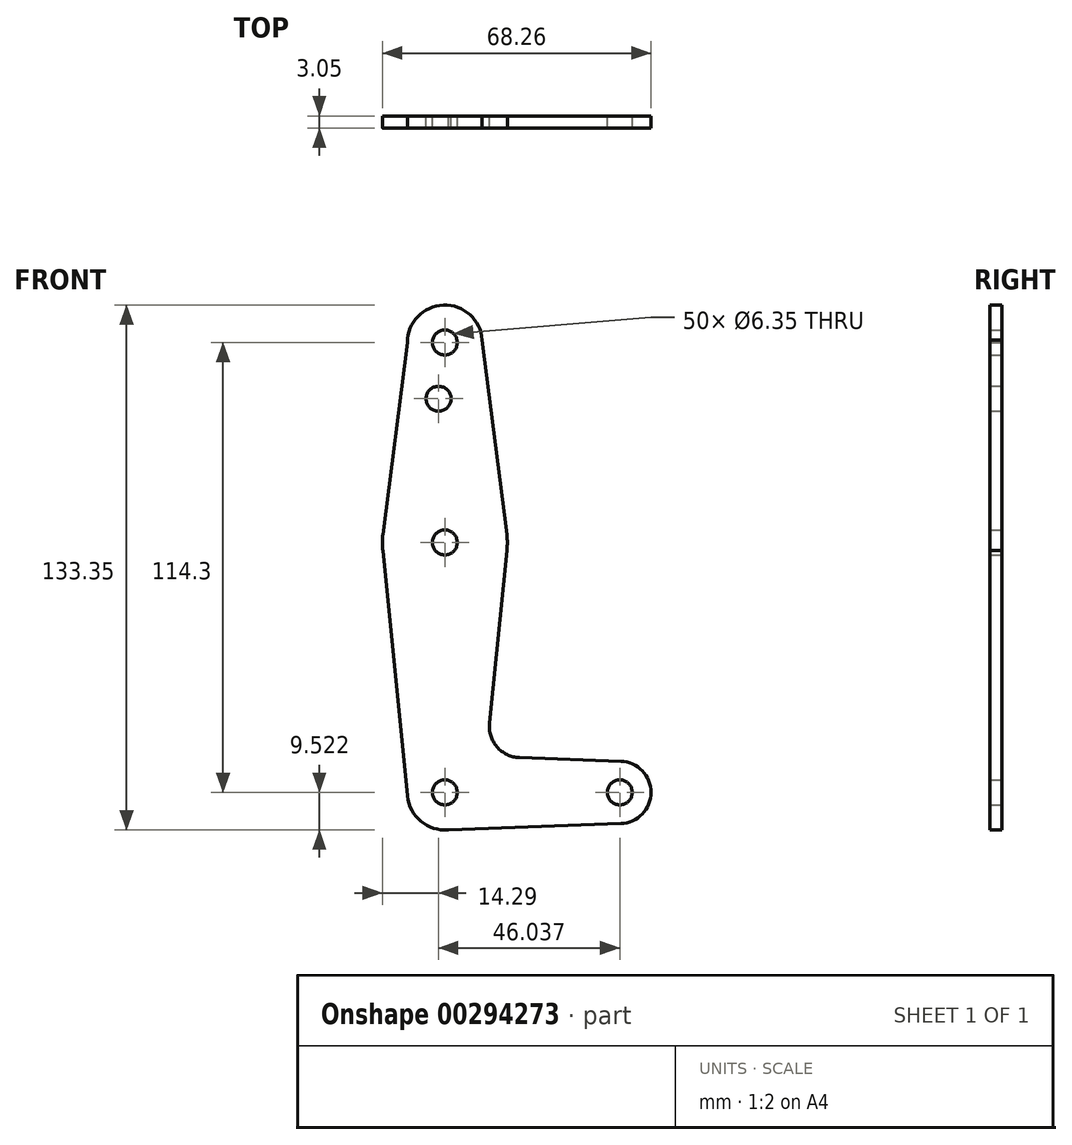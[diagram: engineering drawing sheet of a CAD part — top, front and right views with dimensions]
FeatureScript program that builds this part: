
annotation { "Feature Type Name" : "Feature", "Feature Type Description" : "" }
export const myFeature = defineFeature(function(context is Context, id is Id, definition is map)
    precondition{}
    {
        {
            var Q0;
            Q0=qCreatedBy(makeId("Front.planeOp"),FACE);
            var sketch = newSketch(context, id + "F0", { "sketchPlane" : qUnion([Q0])});
            skCircle(sketch, "E0", {"center": v(-27.75, 77.62) * mm, "radius": 9.53 * mm});
            skCircle(sketch, "E1", {"center": v(-27.75, 26.82) * mm, "radius": 15.88 * mm});
            skCircle(sketch, "E2", {"center": v(-27.75, -36.68) * mm, "radius": 9.53 * mm});
            skCircle(sketch, "E3", {"center": v(16.7, -36.68) * mm, "radius": 7.94 * mm});
            skLineSegment(sketch, "E4", {"start": v(-37.28, 77.62) * mm, "end": v(-43.5, 28.83) * mm});
            skLineSegment(sketch, "E5", {"start": v(-18.25, 78.3) * mm, "end": v(-12, 28.81) * mm});
            skLineSegment(sketch, "E6", {"start": v(-43.5, 24.81) * mm, "end": v(-37.23, -37.63) * mm});
            skLineSegment(sketch, "E7", {"start": v(-12, 24.83) * mm, "end": v(-16.41, -19.09) * mm});
            skLineSegment(sketch, "E8", {"start": v(-8.79, -27.83) * mm, "end": v(16.98, -28.75) * mm});
            skLineSegment(sketch, "E9", {"start": v(-27.98, -46.2) * mm, "end": v(16.98, -44.61) * mm});
            skArc(sketch, "E10.filletArc", {"start": v(-16.41, -19.09) * mm, "mid": v(-14.5, -25.1) * mm, "end": v(-8.79, -27.83) * mm});
            skCircle(sketch, "E11", {"center": v(-27.75, 77.62) * mm, "radius": 3.18 * mm});
            skCircle(sketch, "E12", {"center": v(-27.75, 26.82) * mm, "radius": 3.18 * mm});
            skCircle(sketch, "E13", {"center": v(-27.75, -36.68) * mm, "radius": 3.18 * mm});
            skCircle(sketch, "E14", {"center": v(16.7, -36.68) * mm, "radius": 3.18 * mm});
            skLineSegment(sketch, "E15", {"start": v(-27.75, 77.62) * mm, "end": v(-27.75, -36.68) * mm, "construction": true});
            skLineSegment(sketch, "E16", {"start": v(-27.75, -36.68) * mm, "end": v(16.7, -36.68) * mm, "construction": true});
            skCircle(sketch, "E17", {"center": v(-29.34, 63.35) * mm, "radius": 3.18 * mm});
            skSolve(sketch);
        }
        {
            var Q0;
            Q0 = qSketchRegion(id + "F0", true);
            extrude(context, id + "F1", {"entities" : qUnion([Q0]), "depth" : 3.05 * mm});
        }
    });
